# Revit family: 90 MIDI END FIXED CHIMNEY COWL)
name_source: partatom
category: Generic Models
revit_build: Autodesk Revit 2018 (Build: 20170223_1515(x64)
units: mm (PartAtom-declared; Revit-internal decimal feet)

## family parameters
Always vertical = Yes
Can host rebar = No
Cut with Voids When Loaded = No
Part Type = Normal
Room Calculation Point = No
Round Connector Dimension = Use Diameter
Shared = No
Work Plane-Based = No

## types (1)
- 90 MIDI END FIXED CHIMNEY COWL)
    50X16.5 C-CHANNEL = <By Category>
    50X50 SHS BOX FRAME = <By Category>
    90 MIDI LOUVRE BLADE = <By Category>
    ANGLE = -66.71°
    ARRAY = 8
    HEIGHT = 700 mm  [stored 2.29659 ft]
    LENGTH = 762 mm  [stored 2.5 ft]
    SPACING = 73 mm
    WIDTH = 762 mm  [stored 2.5 ft]

note: [stored X ft] marks values corroborated as IEEE doubles in the binary element streams (Revit-internal decimal feet)

## geometry (parser evidence)
native form markers: Sweep x9
no freeform markers — native parametric forms only
